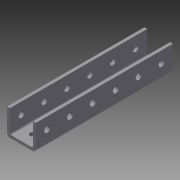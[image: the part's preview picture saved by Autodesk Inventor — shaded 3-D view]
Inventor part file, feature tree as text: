
AUTODESK INVENTOR PART (.ipt)
format: ipt  version: 2014 (Build 180170000, 170)  size: 124,416 bytes
history: native  units: in
note: dims shown in document units (in); Inventor stores cm internally (conversion verified against a paired STEP export)
features: sketch x3, hole x2, extrude x1, pattern_linear x1
ambient origin geometry x8: Origin, YZ Plane, XZ Plane, XY Plane, X Axis, Y Axis, Z Axis, Center Point
bodies: Solid1 (feature_tree)
feature tree (7):
  extrude  "Extrusion1"  Depth=6.0in TaperAngle=0.0deg
  sketch  "Sketch2"  dims[d6=0.5in d7=0.5in]
  sketch  "Sketch3"  dims[d8=0.25in d9=0.75in d10=0.375in d11=0.25in d12=0.5635in d13=1.0in d14=0.8108in d15=0.25in d16=0.75in d17=0.375in d18=0.25in d19=0.5635in d20=1.0in d21=0.8108in d22=2.3622in d24=1.0in]
  hole  "Hole1"  [1 undecoded]
  hole  "Hole2"  [1 undecoded]
  pattern_linear  "Rectangular Pattern1"  [2 undecoded]
  sketch  "Sketch1"  dims[d0=1.25in d1=1.125in d2=0.0625in d3=0.125in d4=6.0in d5=0.0in]
note: 4 required parameter values undecoded (feature->parameter linkage not recoverable at this tier; creation-order binding heuristic only, values carry confidence <= 0.55)
